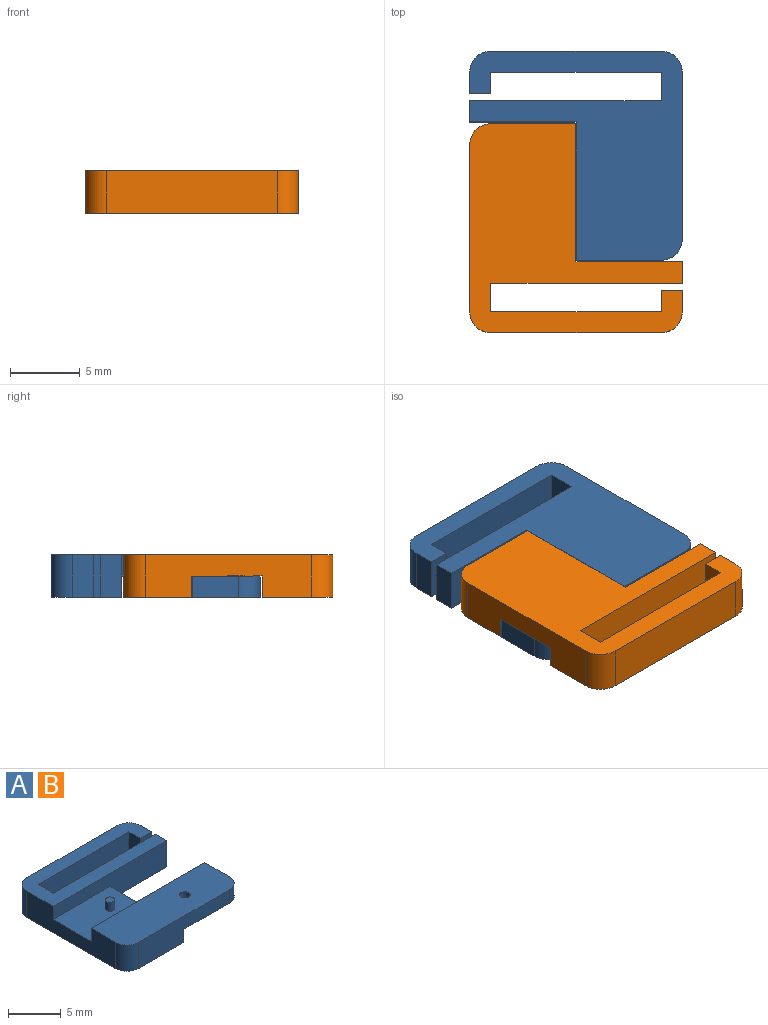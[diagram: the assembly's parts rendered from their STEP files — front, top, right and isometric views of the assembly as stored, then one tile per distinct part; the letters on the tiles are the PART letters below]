
ASSEMBLY  parts=2 mates=1
PART A: 26 faces, bbox 15.2x15x3 mm
  f0: plane 15.24x1.52mm, normal (0,1,0), area 23.2mm2, adj f2,f7,f8,f10,f23
  f1: plane 15.24x14.99mm, normal (0,0,-1), area 125.9mm2, adj f2,f3,f4,f9,f11,f12,f13,f14
  f2: plane 11.94x3.05mm, normal (-1,0,0), area 28.6mm2, adj f0,f1,f3,f8,f11,f21,f22,f23
  f3: cylinder r=1.52mm len=3.05mm, axis (0,0,-1), area 7.3mm2, adj f1,f2,f4,f8
  f4: plane 12.19x3.05mm, normal (0,-1,0), area 27.9mm2, adj f1,f3,f5,f8,f9,f10
  f5: cylinder r=1.52mm len=1.52mm, axis (0,0,-1), area 3.6mm2, adj f4,f7,f8,f10
  f6: cylinder r=0.5mm len=1.52mm, axis (0,0,-1), area 4.8mm2, adj f8,f10
  f7: plane 3.3x1.52mm, normal (1,0,0), area 5mm2, adj f0,f5,f8,f10
  f8: plane 15.24x4.83mm, normal (0,0,1), area 71.8mm2, adj f0,f2,f3,f4,f5,f6,f7
  f9: plane 9.91x1.52mm, normal (1,0,0), area 15.1mm2, adj f1,f4,f10,f11,f23
  f10: plane 7.62x4.83mm, normal (0,0,-1), area 35.5mm2, adj f0,f4,f5,f6,f7,f9
  f11: plane 15.24x3.05mm, normal (0,-1,0), area 34.8mm2, adj f1,f2,f9,f12,f22,f23
  f12: plane 3.05x1.52mm, normal (1,0,0), area 4.6mm2, adj f1,f11,f13,f22
  f13: plane 13.72x3.05mm, normal (0,1,0), area 41.8mm2, adj f1,f12,f14,f22
  f14: plane 3.05x2.03mm, normal (1,0,0), area 6.2mm2, adj f1,f13,f15,f22
  f15: plane 12.19x3.05mm, normal (0,-1,0), area 37.2mm2, adj f1,f14,f16,f22
  f16: plane 3.05x1.53mm, normal (-1,0,0), area 4.7mm2, adj f1,f15,f17,f22
  f17: plane 3.05x1.52mm, normal (0,-1,0), area 4.6mm2, adj f1,f16,f18,f22
  f18: plane 3.05x1.53mm, normal (1,0,0), area 4.7mm2, adj f1,f17,f19,f22
  f19: cylinder r=1.52mm len=3.05mm, axis (0,0,-1), area 7.3mm2, adj f1,f18,f20,f22
  f20: plane 12.19x3.05mm, normal (0,1,0), area 37.2mm2, adj f1,f19,f21,f22
  f21: cylinder r=1.52mm len=3.05mm, axis (0,0,-1), area 7.3mm2, adj f1,f2,f20,f22
  f22: plane 15.24x5.08mm, normal (0,0,1), area 50.9mm2, adj f2,f11,f12,f13,f14,f15,f16,f17
  f23: plane 7.62x5.08mm, normal (0,0,1), area 38mm2, adj f0,f2,f9,f11,f24
  f24: cylinder r=0.46mm len=1.02mm, axis (0,0,-1), area 2.9mm2, adj f23,f25
  f25: plane 0.92x0.92mm, normal (0,0,1), area 0.7mm2, adj f24
PART B: same geometry as A
PLACE A rot(axis=(0,1,0),180deg) t=(13.15,21.02,23.88)mm
PLACE B rot(axis=(1,0,0),180deg) t=(-1.72,23.42,23.88)mm
MATE pin_slot A.f24 <-> B.f6  axis (0,0,-1) through (8.25,24.7,22.35)mm
